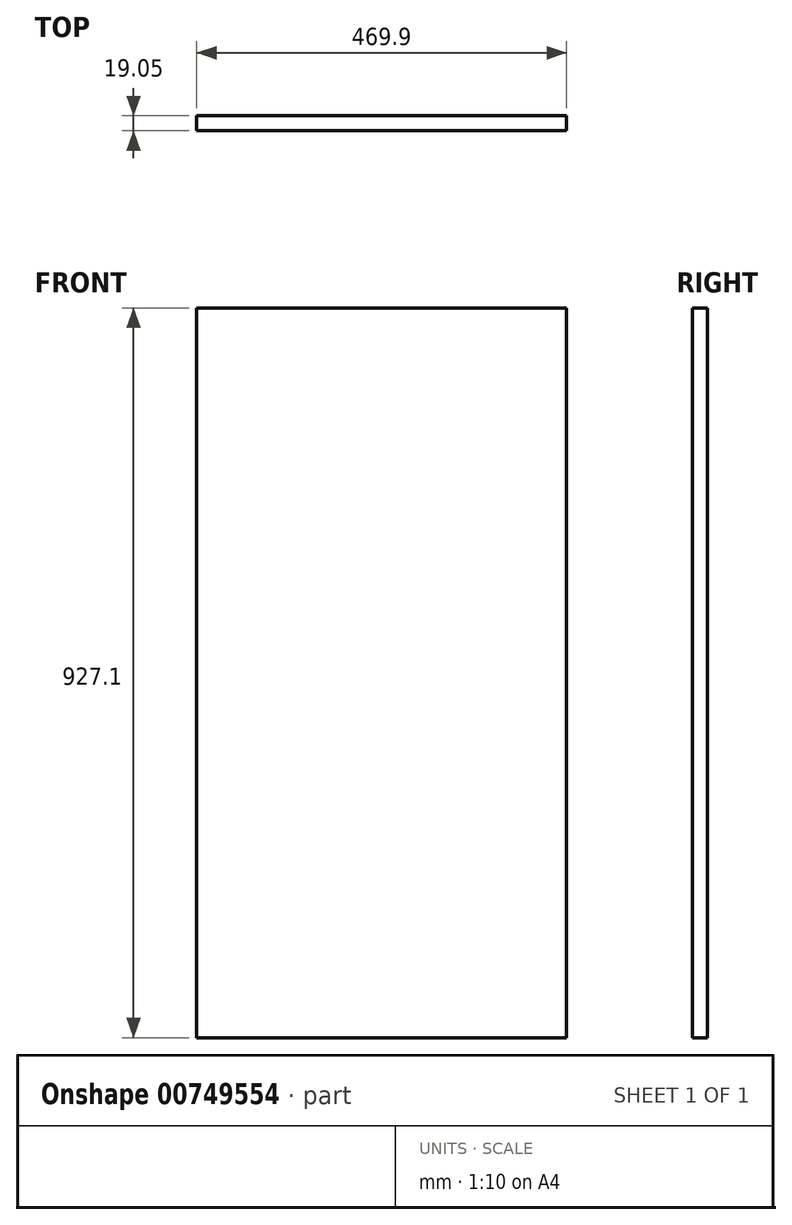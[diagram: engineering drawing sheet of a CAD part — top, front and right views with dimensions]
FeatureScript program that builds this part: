
annotation { "Feature Type Name" : "Feature", "Feature Type Description" : "" }
export const myFeature = defineFeature(function(context is Context, id is Id, definition is map)
    precondition{}
    {
        {
            var Q0;
            Q0=qCreatedBy(makeId("Front.planeOp"),FACE);
            var sketch = newSketch(context, id + "F0", { "sketchPlane" : qUnion([Q0])});
            skLineSegment(sketch, "E0.bottom", {"start": v(234.95, 463.55) * mm, "end": v(-234.95, 463.55) * mm});
            skLineSegment(sketch, "E0.top", {"start": v(234.95, -463.55) * mm, "end": v(-234.95, -463.55) * mm});
            skLineSegment(sketch, "E0.left", {"start": v(234.95, 463.55) * mm, "end": v(234.95, -463.55) * mm});
            skLineSegment(sketch, "E0.right", {"start": v(-234.95, 463.55) * mm, "end": v(-234.95, -463.55) * mm});
            skPoint(sketch, "E0.middle", {"position": v(0, 0) * mm});
            skSolve(sketch);
        }
        {
            var Q0;
            Q0=makeQuery(id+"F0.imprint","IMPRINT",FACE,{"disambiguationData":[TD([[makeQuery(id+"F0.imprint","IMPRINT",EDGE,{"derivedFrom":sQuery(id+"F0.wireOp",EDGE,"E0.bottom")}),1.0]])]});
            extrude(context, id + "F1", {"entities" : qUnion([Q0]), "depth" : 19.05 * mm, "offsetDistance" : 25.4 * mm});
        }
    });
